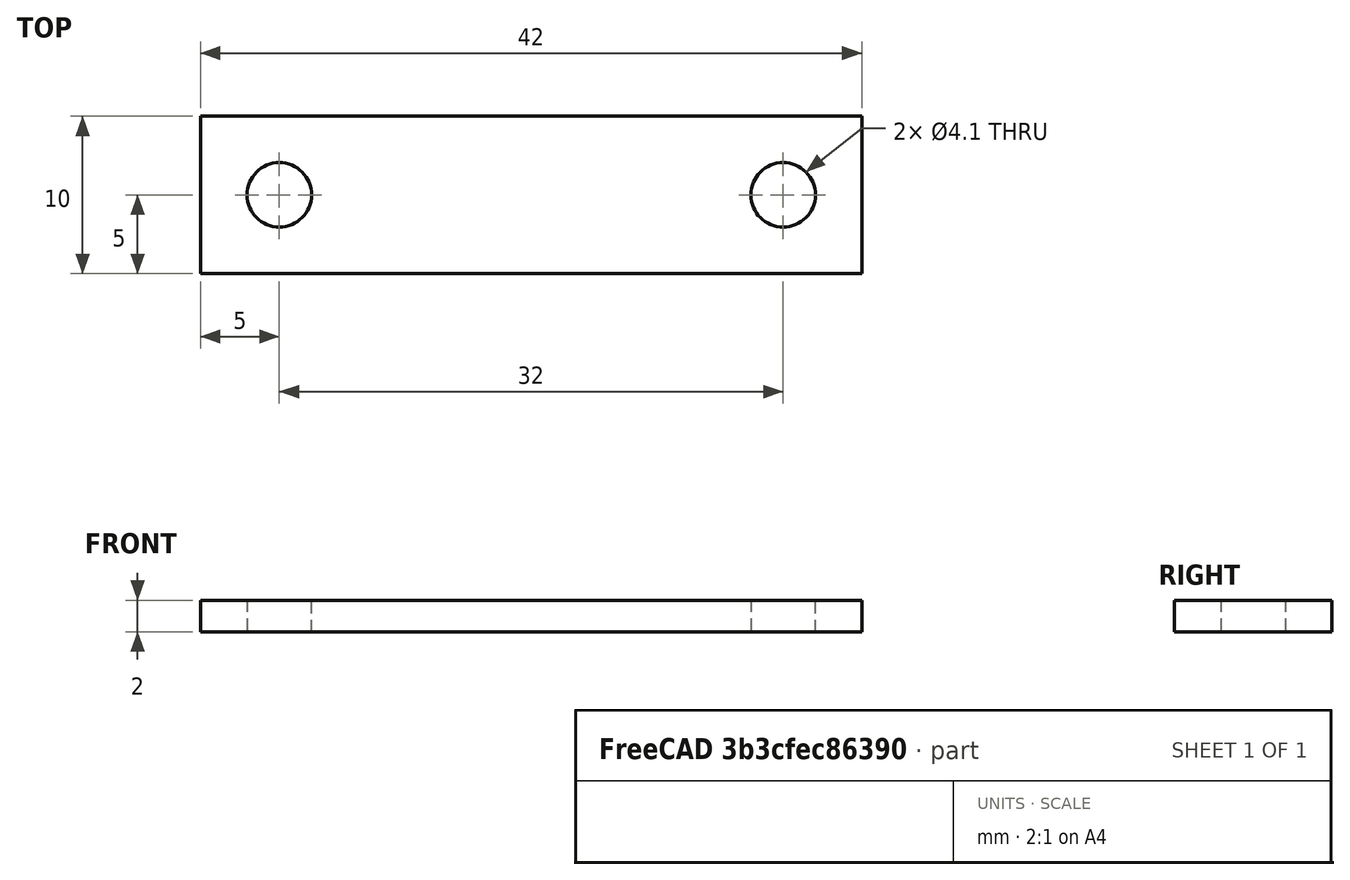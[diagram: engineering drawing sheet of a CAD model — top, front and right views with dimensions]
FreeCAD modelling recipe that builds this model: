
FCSTD DOCUMENT  (FreeCAD 0.21R33771 (Git))
Label: Frame75Parts
License: All rights reserved
LicenseURL: https://en.wikipedia.org/wiki/All_rights_reserved
objects: PartDesign::Plane×1, Sketcher::SketchObject×1, PartDesign::Pad×1, PartDesign::Body×1
note: 5 computed .brp shape members not serialized (recipe doc carries the construction recipe); baked Part::Feature solids carry a one-line shape summary decoded from their .brp

FEATURE [PartDesign::Plane] DatumPlane001  label="DatumPlane"
  Length = 89.4097
  MapMode = 5
  ResizeMode = 0
  Support = -> [XY_Plane001]
  Width = 62.4097
FEATURE [Sketcher::SketchObject] Sketch004  label="SensorCoverS"
  FullyConstrained = true
  MapMode = 5
  Support = -> [DatumPlane001]
  sketch-geometry (6):
    g0: LineSegment StartX=10 StartY=20 StartZ=0 EndX=10 EndY=10 EndZ=0
    g1: LineSegment StartX=10 StartY=10 StartZ=0 EndX=52 EndY=10 EndZ=0
    g2: LineSegment StartX=52 StartY=10 StartZ=0 EndX=52 EndY=20 EndZ=0
    g3: LineSegment StartX=52 StartY=20 StartZ=0 EndX=10 EndY=20 EndZ=0
    g4: Circle CenterX=15 CenterY=15 CenterZ=0 NormalX=0 NormalY=0 NormalZ=1 AngleXU=0 Radius=2.05
    g5: Circle CenterX=47 CenterY=15 CenterZ=0 NormalX=0 NormalY=0 NormalZ=1 AngleXU=0 Radius=2.05
  constraints (18):
    c: Vertical(g0)
    c: Coincident(g0,g1)
    c: Horizontal(g1)
    c: Coincident(g1,g2)
    c: Vertical(g2)
    c: Coincident(g2,g3)
    c: Horizontal(g3)
    c: DistanceY(g2,g2) = 10
    c: Equal(g4,g5)
    c: Diameter(g4) = 4.1
    c: DistanceX(g4,g5) = 32
    c: Distance(g4,g1) = 5
    c: Distance(g5,g1) = 5
    c: Coincident(g3,g0)
    c: Distance(g4,g0) = 5
    c: Distance(g5,g2) = 5
    c: DistanceX(g0,g-1) = -10
    c: DistanceY(g0,g-1) = -10
FEATURE [PartDesign::Pad] Pad002  label="SensorCover001"
  Direction = (0,0,1)
  Length = 2
  Length2 = 10
  Profile = -> Sketch004
  ReferenceAxis = -> Sketch004 [N_Axis]
  Type = 0
FEATURE [PartDesign::Body] Body001  label="SensorCover"
  Group = -> [DatumPlane001,Sketch004,Pad002]
  Origin = -> Origin001
  Tip = -> Pad002
